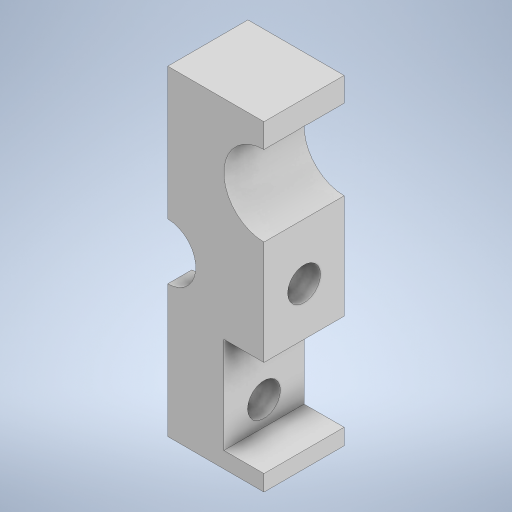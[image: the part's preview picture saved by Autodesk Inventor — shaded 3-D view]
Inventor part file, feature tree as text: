
AUTODESK INVENTOR PART (.ipt)
format: ipt  version: 2023 (Build 270158000, 158)  size: 322,048 bytes
history: native  units: mm
features: extrude x7, sketch x7, plane x1
ambient origin geometry x8: Origin, YZ Plane, XZ Plane, XY Plane, X Axis, Y Axis, Z Axis, Center Point
bodies: Solid1 (feature_tree)
feature tree (15):
  extrude  "Extrusion1"  Depth=20.0mm
  plane  "Work Plane1"
  extrude  "Extrusion2"  Depth=2.0mm
  extrude  "Extrusion3"  Depth=4.0mm
  extrude  "Extrusion4"  Depth=5.0mm TaperAngle=0.0deg
  extrude  "Extrusion5"  Depth=5.0mm TaperAngle=0.0deg
  extrude  "Extrusion6"  Depth=8.0mm TaperAngle=0.0deg
  extrude  "Extrusion7"  Depth=10.0mm
  sketch  "Sketch1"  dims[d0=20.0mm d1=20.0mm]
  sketch  "Sketch2"  dims[d2=4.0mm d6=2.0mm]
  sketch  "Sketch3"  dims[d7=2.0mm d8=4.0mm]
  sketch  "Sketch4"  dims[d9=2.0mm d10=5.0mm d11=0.0mm]
  sketch  "Sketch5"  dims[d12=5.0mm d13=2.0mm d14=0.0mm]
  sketch  "Sketch6"  dims[d15=3.5mm d16=8.0mm d17=0.0mm]
  sketch  "Sketch7"  dims[d18=2.05mm d19=2.05mm d20=2.5mm d21=2.5mm d22=2.5mm d23=2.5mm d24=25.0mm d25=0.0mm d30=5.0mm d31=0.0mm d32=2.5mm d33=1.0mm d34=6.0mm d35=5.0mm d36=4.0mm d37=5.0mm d38=0.0mm d39=2.5mm d40=10.0mm d41=2.05mm d42=12.0mm d43=0.0mm d44=6.0mm]
